# Revit family: Genie_Site_ArticulatingBoom_(Z-45XC)a
name_source: partatom
category: Site
revit_build: Autodesk Revit 2018 (Build: 20170223_1515(x64)
units: mm (PartAtom-declared; Revit-internal decimal feet)

## family parameters
Always vertical = Yes
Cut with Voids When Loaded = No
OmniClass Number = 23.50.85.17.11
OmniClass Title = Electric and Battery Telescoping Platforms
Part Type = Normal
Round Connector Dimension = Use Diameter
Shared = No
Work Plane-Based = No

## types (1)
- Z-45XC
    Assembly Code = E1030900
    AssetType = Fixed
    BIMObjectName = Genie_Site_ArticulatingBoom_(Z-45XC)
    ClassificationName = Uniclass2015
    ClassificationValue = Pr_65_80_47_95
    Color = Grey & Blue
    Cost = 0 $
    Description = The Genie® Z®-45 XC™ articulating boom is the redesigned Xtra Capacity™ version of the popular rough-terrain Genie Z-45/25 J RT diesel powered articulating boom. It’s the first Genie XC articulating boom model, boasting the benefits of a dual-envelope design to provide an unrestricted platform capacity of 660 lb (300 kg) and a restricted capacity of 1,000 lb (454 kg).
    DocumentationLiterature = https://www.genielift.com
    DocumentationTechnical = https://www.genielift.com
    DurationUnit = Years
    ExpectedLife = 0
    Features = Load sense technology for accurate load weighing and zero-load field calibration. Rough terrain capabilities include 45% gradeability. Updated oscillating system boasts faster response time. Commonality in design and accessories with other Genie booms for easy parts stocking.
    Finish = Painted Steel
    IfcExportAs = IfcTransportElement
    IfcExportType = IfcTransportElementType
    Keynote = X
    Manufacturer = Genie
    ManufacturerName = Genie
    Material = Painted Steel
    Model = Genie - Articulating Boom
    ModelNumber = Z-45XC
    ModelReference = Genie - Articulating Boom
    NBSDescription = Vertical lifting platforms
    NBSObjectName = Genie - Vertical lifting platforms
    NBSReference = 90-80-65/350
    NominalDepth = 2490 mm
    NominalHeight = 2510 mm
    NominalLength = 8000 mm
    ProductionYear = 2019
    ReplacementCost = 0
    Size = 8.00m x 2.51m x 2.49m
    Type Comments = Z-45XC
    TypeName = Genie - Articulating Boom
    URL = http://www.genielift.co.uk
    WarrantyDurationLabor = 0
    WarrantyDurationParts = 0
    WarrantyDurationUnit = Years
    WarrantyGuarantorLabor = http://www.genielift.co.uk
    WarrantyGuarantorParts = http://www.genielift.co.uk
    _BSBibleVersion = 16
    _BimSpecGuid = 0
    _CurrentRevision = 1
    _DistributedBy = www.bimstore.co.uk

## geometry (parser evidence)
native form markers: Sweep x37
no freeform markers — native parametric forms only
